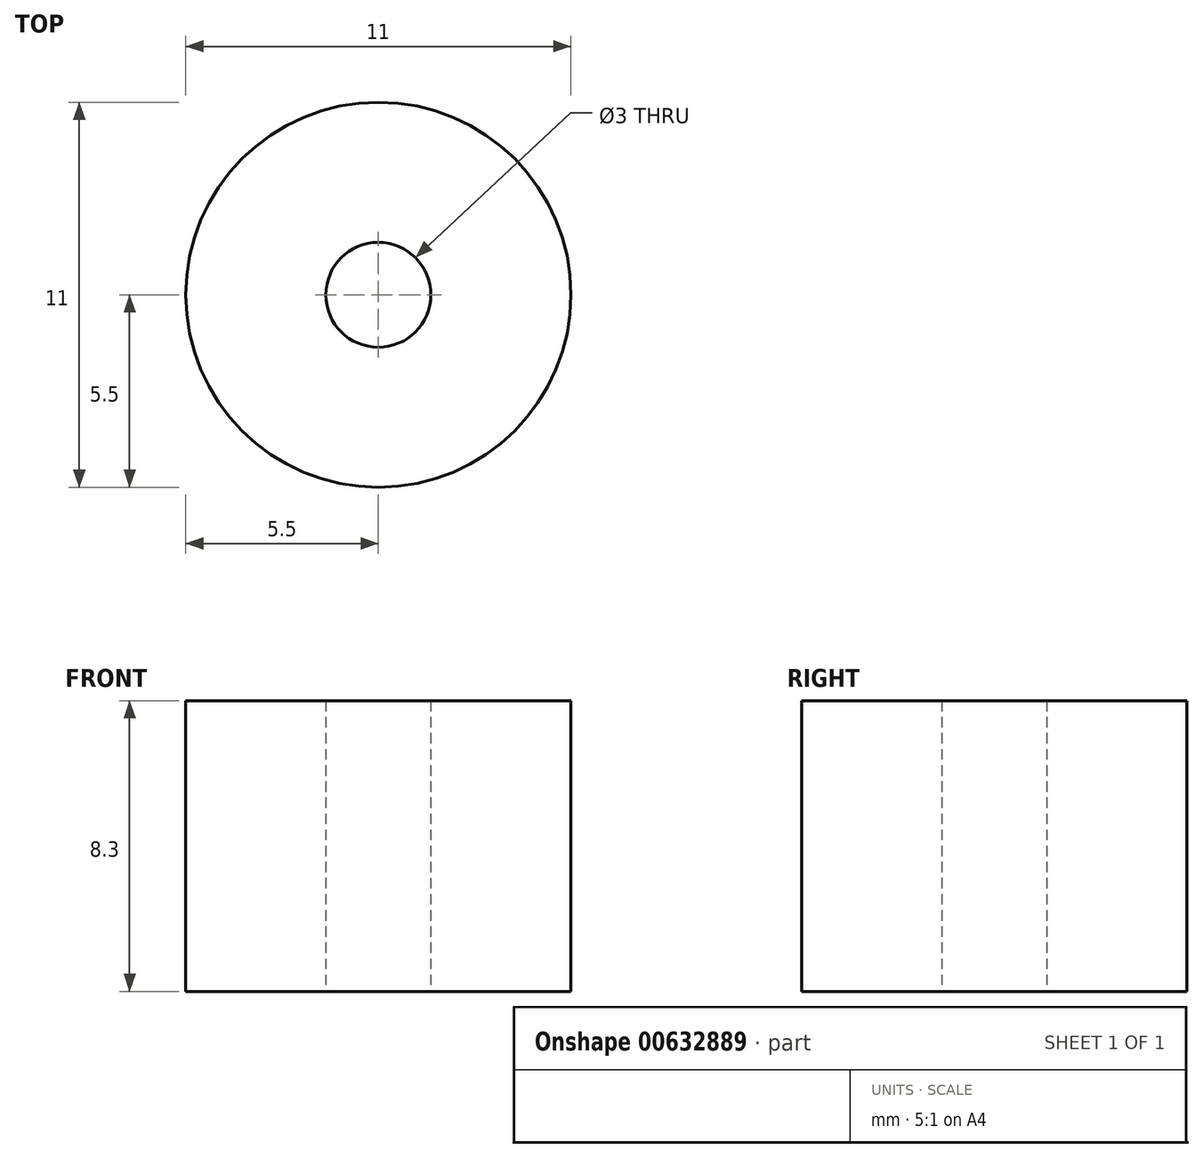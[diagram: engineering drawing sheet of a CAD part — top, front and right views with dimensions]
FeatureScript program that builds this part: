
annotation { "Feature Type Name" : "Feature", "Feature Type Description" : "" }
export const myFeature = defineFeature(function(context is Context, id is Id, definition is map)
    precondition{}
    {
        {
            var Q0;
            Q0=qCreatedBy(makeId("Top.planeOp"),FACE);
            var sketch = newSketch(context, id + "F0", { "sketchPlane" : qUnion([Q0])});
            skCircle(sketch, "E0", {"center": v(0, 0) * mm, "radius": 5.5 * mm});
            skCircle(sketch, "E1", {"center": v(0, 0) * mm, "radius": 4.75 * mm});
            skCircle(sketch, "E2", {"center": v(0, 0) * mm, "radius": 1.5 * mm});
            skSolve(sketch);
        }
        {
            var Q0;
            Q0=makeQuery(id+"F0.imprint","IMPRINT",FACE,{"disambiguationData":[TD([[makeQuery(id+"F0.imprint","IMPRINT",EDGE,{"derivedFrom":sQuery(id+"F0.wireOp",EDGE,"E1")}),1.0]])]});
            var Q1;
            Q1=makeQuery(id+"F0.imprint","IMPRINT",FACE,{"disambiguationData":[TD([[makeQuery(id+"F0.imprint","IMPRINT",EDGE,{"derivedFrom":sQuery(id+"F0.wireOp",EDGE,"E0")}),1.0]])]});
            extrude(context, id + "F1", {"entities" : qUnion([Q0, Q1]), "depth" : 8.3 * mm, "offsetDistance" : 25 * mm});
        }
    });
